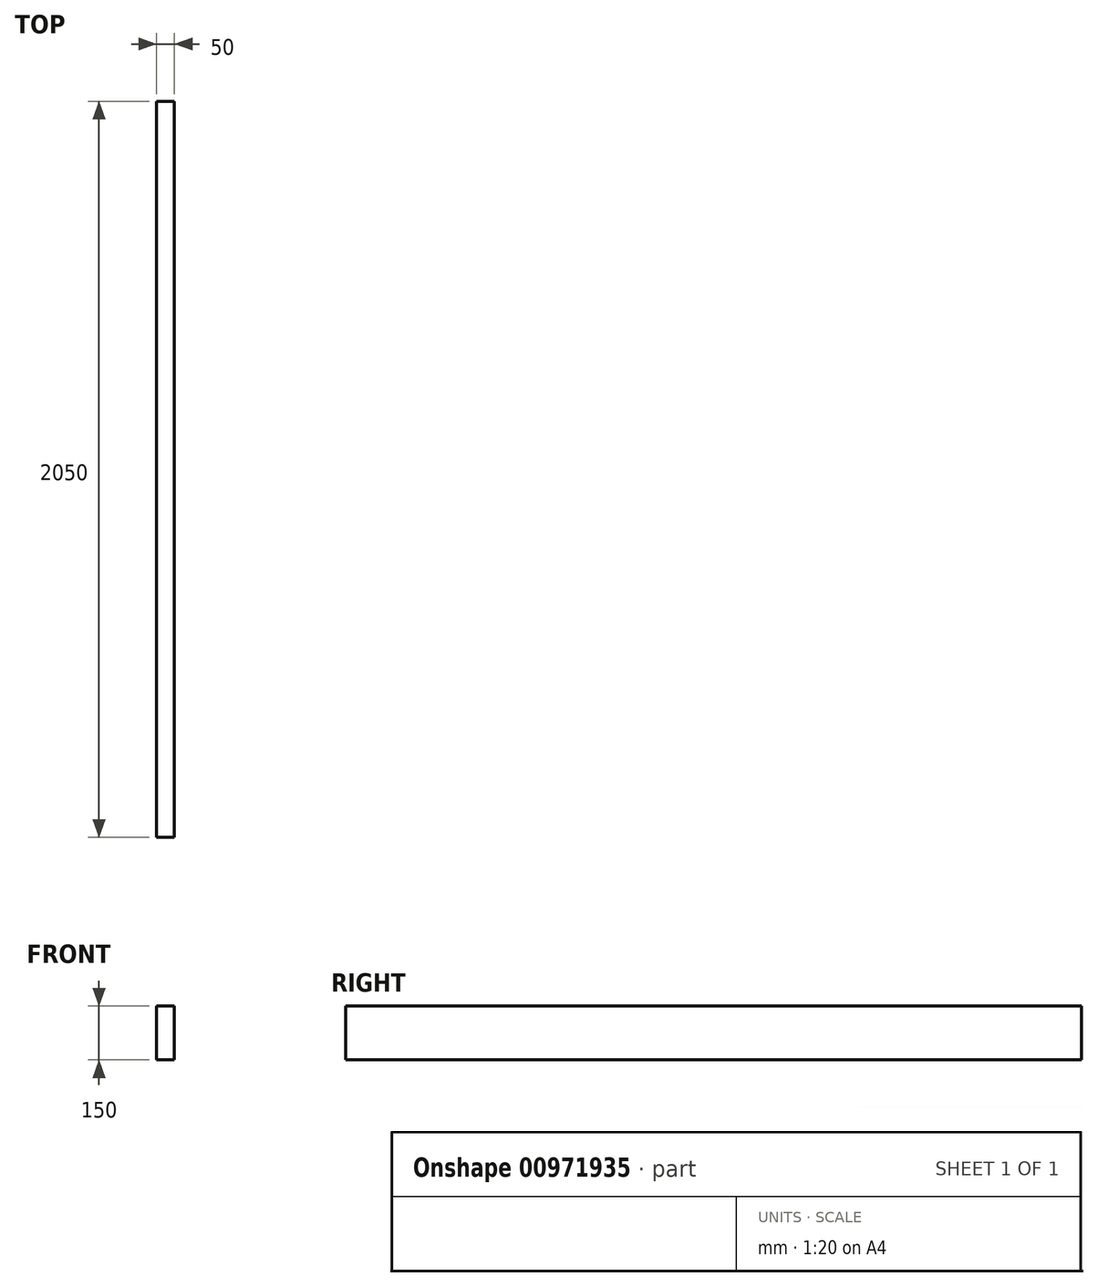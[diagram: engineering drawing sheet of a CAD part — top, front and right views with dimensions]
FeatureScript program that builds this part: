
annotation { "Feature Type Name" : "Feature", "Feature Type Description" : "" }
export const myFeature = defineFeature(function(context is Context, id is Id, definition is map)
    precondition{}
    {
        {
            var Q0;
            Q0=qCreatedBy(makeId("Front.planeOp"),FACE);
            var sketch = newSketch(context, id + "F0", { "sketchPlane" : qUnion([Q0])});
            skLineSegment(sketch, "E0.bottom", {"start": v(25, -75) * mm, "end": v(-25, -75) * mm});
            skLineSegment(sketch, "E0.top", {"start": v(25, 75) * mm, "end": v(-25, 75) * mm});
            skLineSegment(sketch, "E0.left", {"start": v(25, -75) * mm, "end": v(25, 75) * mm});
            skLineSegment(sketch, "E0.right", {"start": v(-25, -75) * mm, "end": v(-25, 75) * mm});
            skPoint(sketch, "E0.middle", {"position": v(0, 0) * mm});
            skSolve(sketch);
        }
        {
            var Q0;
            Q0 = qSketchRegion(id + "F0", true);
            extrude(context, id + "F1", {"entities" : qUnion([Q0]), "depth" : 2050 * mm, "offsetDistance" : 25 * mm});
        }
    });
